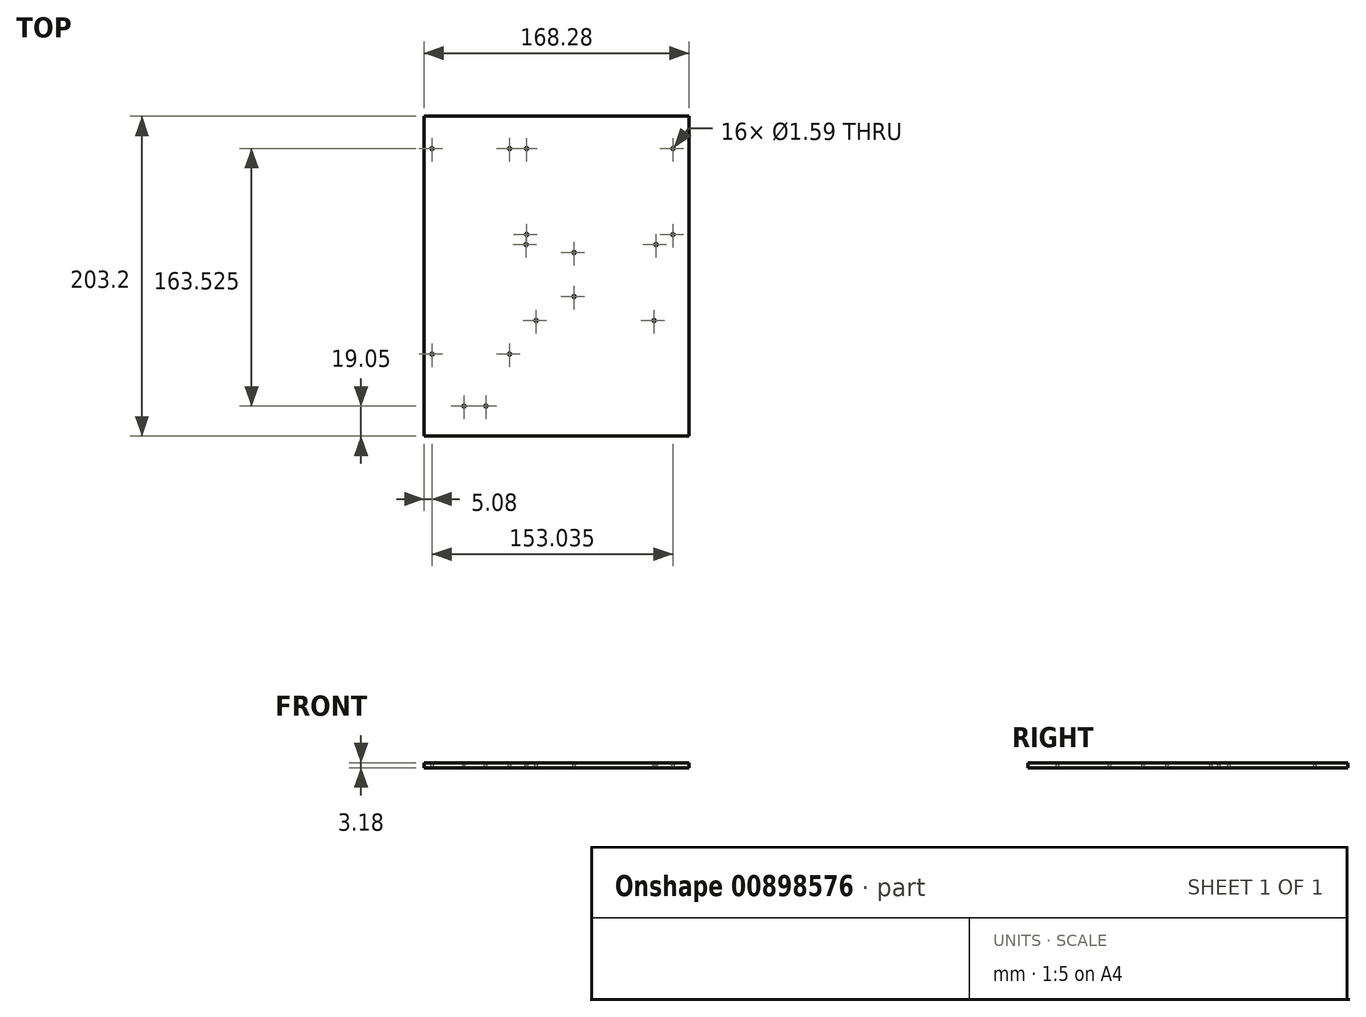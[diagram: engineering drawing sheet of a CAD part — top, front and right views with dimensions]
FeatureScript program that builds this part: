
annotation { "Feature Type Name" : "Feature", "Feature Type Description" : "" }
export const myFeature = defineFeature(function(context is Context, id is Id, definition is map)
    precondition{}
    {
        {
            var Q0;
            Q0=qCreatedBy(makeId("Top.planeOp"),FACE);
            var sketch = newSketch(context, id + "F0", { "sketchPlane" : qUnion([Q0])});
            skLineSegment(sketch, "E0.bottom", {"start": v(0, 203.2) * mm, "end": v(168.28, 203.2) * mm});
            skLineSegment(sketch, "E0.top", {"start": v(0, 0) * mm, "end": v(168.28, 0) * mm});
            skLineSegment(sketch, "E0.left", {"start": v(0, 203.2) * mm, "end": v(0, 0) * mm});
            skLineSegment(sketch, "E0.right", {"start": v(168.28, 203.2) * mm, "end": v(168.28, 0) * mm});
            skSolve(sketch);
        }
        {
            var Q0;
            Q0=qCreatedBy(makeId("Top.planeOp"),FACE);
            var sketch = newSketch(context, id + "F1", { "sketchPlane" : qUnion([Q0])});
            skLineSegment(sketch, "E1", {"start": v(147.4, 121.62) * mm, "end": v(64.85, 121.62) * mm, "construction": true});
            skLineSegment(sketch, "E2", {"start": v(146.13, 73.36) * mm, "end": v(71.2, 73.36) * mm, "construction": true});
            skLineSegment(sketch, "E3", {"start": v(95.33, 88.6) * mm, "end": v(95.33, 116.54) * mm, "construction": true});
            skCircle(sketch, "E4", {"center": v(146.13, 73.36) * mm, "radius": 0.8 * mm});
            skCircle(sketch, "E5", {"center": v(147.4, 121.62) * mm, "radius": 0.8 * mm});
            skCircle(sketch, "E6", {"center": v(95.33, 116.54) * mm, "radius": 0.8 * mm});
            skCircle(sketch, "E7", {"center": v(95.33, 88.6) * mm, "radius": 0.8 * mm});
            skCircle(sketch, "E8", {"center": v(64.85, 121.62) * mm, "radius": 0.8 * mm});
            skCircle(sketch, "E9", {"center": v(71.2, 73.36) * mm, "radius": 0.8 * mm});
            skLineSegment(sketch, "E10", {"start": v(147.4, 121.62) * mm, "end": v(147.4, 73.36) * mm, "construction": true});
            skLineSegment(sketch, "E11", {"start": v(147.4, 73.36) * mm, "end": v(146.13, 73.36) * mm, "construction": true});
            skSolve(sketch);
        }
        {
            var Q0;
            Q0=makeQuery(id+"F0.imprint","IMPRINT",FACE,{"disambiguationData":[TD([[makeQuery(id+"F0.imprint","IMPRINT",EDGE,{"derivedFrom":sQuery(id+"F0.wireOp",EDGE,"E0.bottom")}),-1.0]])]});
            extrude(context, id + "F2", {"entities" : qUnion([Q0]), "oppositeDirection" : true, "depth" : 3.17 * mm, "offsetDistance" : 25.4 * mm});
        }
        {
            var Q0;
            Q0=makeQuery(id+"F1.imprint","IMPRINT",FACE,{"disambiguationData":[TD([[makeQuery(id+"F1.imprint","IMPRINT",EDGE,{"derivedFrom":sQuery(id+"F1.wireOp",EDGE,"E9")}),1.0]])]});
            var Q1;
            Q1=makeQuery(id+"F1.imprint","IMPRINT",FACE,{"disambiguationData":[TD([[makeQuery(id+"F1.imprint","IMPRINT",EDGE,{"derivedFrom":sQuery(id+"F1.wireOp",EDGE,"E8")}),1.0]])]});
            var Q2;
            Q2=makeQuery(id+"F1.imprint","IMPRINT",FACE,{"disambiguationData":[TD([[makeQuery(id+"F1.imprint","IMPRINT",EDGE,{"derivedFrom":sQuery(id+"F1.wireOp",EDGE,"E6")}),1.0]])]});
            var Q3;
            Q3=makeQuery(id+"F1.imprint","IMPRINT",FACE,{"disambiguationData":[TD([[makeQuery(id+"F1.imprint","IMPRINT",EDGE,{"derivedFrom":sQuery(id+"F1.wireOp",EDGE,"E4")}),1.0]])]});
            var Q4;
            Q4=makeQuery(id+"F1.imprint","IMPRINT",FACE,{"disambiguationData":[TD([[makeQuery(id+"F1.imprint","IMPRINT",EDGE,{"derivedFrom":sQuery(id+"F1.wireOp",EDGE,"E5")}),1.0]])]});
            var Q5;
            Q5=makeQuery(id+"F1.imprint","IMPRINT",FACE,{"disambiguationData":[TD([[makeQuery(id+"F1.imprint","IMPRINT",EDGE,{"derivedFrom":sQuery(id+"F1.wireOp",EDGE,"E7")}),1.0]])]});
            extrude(context, id + "F3", {"entities" : qUnion([Q0, Q1, Q2, Q3, Q4, Q5]), "operationType" : NewBodyOperationType.REMOVE, "oppositeDirection" : true, "depth" : 25.4 * mm, "offsetDistance" : 25.4 * mm});
        }
        {
            var Q0;
            Q0=qCreatedBy(makeId("Top.planeOp"),FACE);
            var sketch = newSketch(context, id + "F4", { "sketchPlane" : qUnion([Q0])});
            skLineSegment(sketch, "E12.bottom", {"start": v(65.15, 182.58) * mm, "end": v(158.12, 182.58) * mm, "construction": true});
            skLineSegment(sketch, "E12.top", {"start": v(65.15, 127.97) * mm, "end": v(158.12, 127.97) * mm, "construction": true});
            skLineSegment(sketch, "E12.left", {"start": v(65.15, 182.58) * mm, "end": v(65.15, 127.97) * mm, "construction": true});
            skLineSegment(sketch, "E12.right", {"start": v(158.12, 182.58) * mm, "end": v(158.12, 127.97) * mm, "construction": true});
            skCircle(sketch, "E13", {"center": v(65.15, 127.97) * mm, "radius": 0.8 * mm});
            skCircle(sketch, "E14", {"center": v(65.15, 182.58) * mm, "radius": 0.8 * mm});
            skCircle(sketch, "E15", {"center": v(158.12, 182.58) * mm, "radius": 0.8 * mm});
            skCircle(sketch, "E16", {"center": v(158.12, 127.97) * mm, "radius": 0.8 * mm});
            skSolve(sketch);
        }
        {
            var Q0;
            Q0=makeQuery(id+"F4.imprint","IMPRINT",FACE,{"disambiguationData":[TD([[makeQuery(id+"F4.imprint","IMPRINT",EDGE,{"derivedFrom":sQuery(id+"F4.wireOp",EDGE,"E13")}),1.0]])]});
            var Q1;
            Q1=makeQuery(id+"F4.imprint","IMPRINT",FACE,{"disambiguationData":[TD([[makeQuery(id+"F4.imprint","IMPRINT",EDGE,{"derivedFrom":sQuery(id+"F4.wireOp",EDGE,"E16")}),1.0]])]});
            var Q2;
            Q2=makeQuery(id+"F4.imprint","IMPRINT",FACE,{"disambiguationData":[TD([[makeQuery(id+"F4.imprint","IMPRINT",EDGE,{"derivedFrom":sQuery(id+"F4.wireOp",EDGE,"E15")}),1.0]])]});
            var Q3;
            Q3=makeQuery(id+"F4.imprint","IMPRINT",FACE,{"disambiguationData":[TD([[makeQuery(id+"F4.imprint","IMPRINT",EDGE,{"derivedFrom":sQuery(id+"F4.wireOp",EDGE,"E14")}),1.0]])]});
            extrude(context, id + "F5", {"entities" : qUnion([Q0, Q1, Q2, Q3]), "operationType" : NewBodyOperationType.REMOVE, "oppositeDirection" : true, "depth" : 25.4 * mm, "offsetDistance" : 25.4 * mm});
        }
        {
            var Q0;
            Q0=qCreatedBy(makeId("Top.planeOp"),FACE);
            var sketch = newSketch(context, id + "F6", { "sketchPlane" : qUnion([Q0])});
            skLineSegment(sketch, "E17.bottom", {"start": v(5.08, 182.58) * mm, "end": v(54.33, 182.58) * mm, "construction": true});
            skLineSegment(sketch, "E17.top", {"start": v(5.08, 52.07) * mm, "end": v(54.33, 52.07) * mm, "construction": true});
            skLineSegment(sketch, "E17.left", {"start": v(5.08, 182.58) * mm, "end": v(5.08, 52.07) * mm, "construction": true});
            skLineSegment(sketch, "E17.right", {"start": v(54.33, 182.58) * mm, "end": v(54.33, 52.07) * mm, "construction": true});
            skCircle(sketch, "E18", {"center": v(54.33, 182.58) * mm, "radius": 0.8 * mm});
            skCircle(sketch, "E19", {"center": v(5.08, 182.58) * mm, "radius": 0.8 * mm});
            skCircle(sketch, "E20", {"center": v(5.08, 52.07) * mm, "radius": 0.8 * mm});
            skCircle(sketch, "E21", {"center": v(54.33, 52.07) * mm, "radius": 0.8 * mm});
            skSolve(sketch);
        }
        {
            var Q0;
            Q0=makeQuery(id+"F6.imprint","IMPRINT",FACE,{"disambiguationData":[TD([[makeQuery(id+"F6.imprint","IMPRINT",EDGE,{"derivedFrom":sQuery(id+"F6.wireOp",EDGE,"E20")}),1.0]])]});
            var Q1;
            Q1=makeQuery(id+"F6.imprint","IMPRINT",FACE,{"disambiguationData":[TD([[makeQuery(id+"F6.imprint","IMPRINT",EDGE,{"derivedFrom":sQuery(id+"F6.wireOp",EDGE,"E21")}),1.0]])]});
            var Q2;
            Q2=makeQuery(id+"F6.imprint","IMPRINT",FACE,{"disambiguationData":[TD([[makeQuery(id+"F6.imprint","IMPRINT",EDGE,{"derivedFrom":sQuery(id+"F6.wireOp",EDGE,"E18")}),1.0]])]});
            var Q3;
            Q3=makeQuery(id+"F6.imprint","IMPRINT",FACE,{"disambiguationData":[TD([[makeQuery(id+"F6.imprint","IMPRINT",EDGE,{"derivedFrom":sQuery(id+"F6.wireOp",EDGE,"E19")}),1.0]])]});
            extrude(context, id + "F7", {"entities" : qUnion([Q0, Q1, Q2, Q3]), "operationType" : NewBodyOperationType.REMOVE, "oppositeDirection" : true, "depth" : 25.4 * mm, "offsetDistance" : 25.4 * mm});
        }
        {
            var Q0;
            Q0=qCreatedBy(makeId("Top.planeOp"),FACE);
            var sketch = newSketch(context, id + "F8", { "sketchPlane" : qUnion([Q0])});
            skLineSegment(sketch, "E22", {"start": v(25.4, 19.05) * mm, "end": v(39.32, 19.05) * mm, "construction": true});
            skCircle(sketch, "E23", {"center": v(25.4, 19.05) * mm, "radius": 0.8 * mm});
            skCircle(sketch, "E24", {"center": v(39.32, 19.05) * mm, "radius": 0.8 * mm});
            skSolve(sketch);
        }
        {
            var Q0;
            Q0=makeQuery(id+"F8.imprint","IMPRINT",FACE,{"disambiguationData":[TD([[makeQuery(id+"F8.imprint","IMPRINT",EDGE,{"derivedFrom":sQuery(id+"F8.wireOp",EDGE,"E23")}),1.0]])]});
            var Q1;
            Q1=makeQuery(id+"F8.imprint","IMPRINT",FACE,{"disambiguationData":[TD([[makeQuery(id+"F8.imprint","IMPRINT",EDGE,{"derivedFrom":sQuery(id+"F8.wireOp",EDGE,"E24")}),1.0]])]});
            extrude(context, id + "F9", {"entities" : qUnion([Q0, Q1]), "operationType" : NewBodyOperationType.REMOVE, "oppositeDirection" : true, "depth" : 25.4 * mm, "offsetDistance" : 25.4 * mm});
        }
    });
